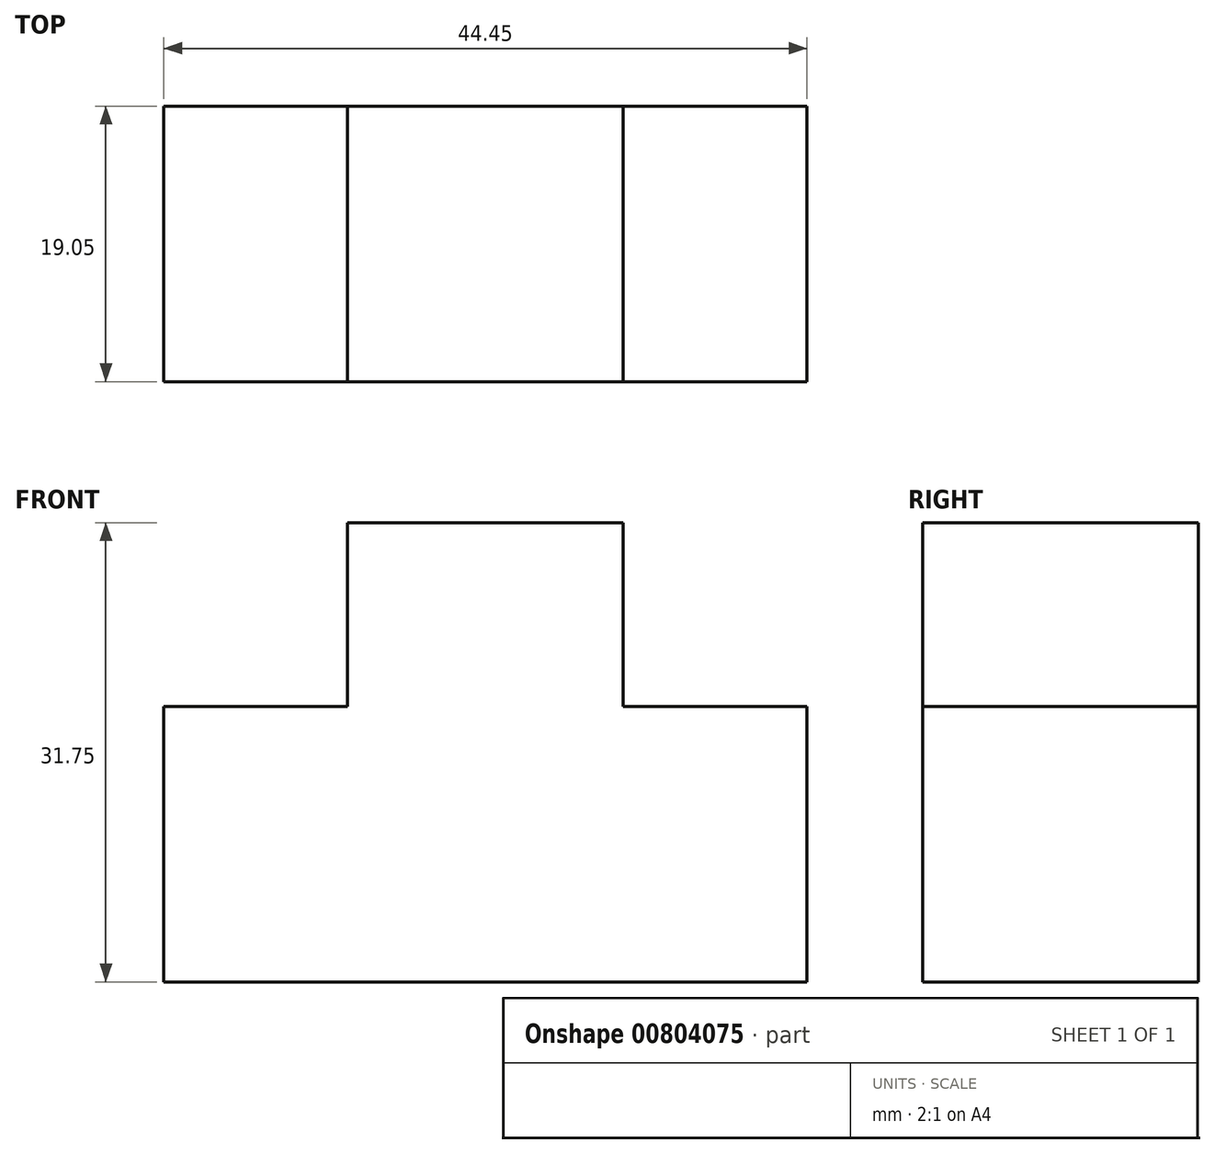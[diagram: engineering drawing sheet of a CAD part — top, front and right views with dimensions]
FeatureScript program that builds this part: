
annotation { "Feature Type Name" : "Feature", "Feature Type Description" : "" }
export const myFeature = defineFeature(function(context is Context, id is Id, definition is map)
    precondition{}
    {
        {
            var Q0;
            Q0=qCreatedBy(makeId("Front.planeOp"),FACE);
            var sketch = newSketch(context, id + "F0", { "sketchPlane" : qUnion([Q0])});
            skLineSegment(sketch, "E0", {"start": v(0, 0) * mm, "end": v(44.45, 0) * mm});
            skLineSegment(sketch, "E1", {"start": v(44.45, 0) * mm, "end": v(44.45, 19.05) * mm});
            skLineSegment(sketch, "E2", {"start": v(44.45, 19.05) * mm, "end": v(31.75, 19.05) * mm});
            skLineSegment(sketch, "E3", {"start": v(31.75, 19.05) * mm, "end": v(31.75, 31.75) * mm});
            skLineSegment(sketch, "E4", {"start": v(31.75, 31.75) * mm, "end": v(12.7, 31.75) * mm});
            skLineSegment(sketch, "E5", {"start": v(12.7, 31.75) * mm, "end": v(12.7, 19.05) * mm});
            skLineSegment(sketch, "E6", {"start": v(12.7, 19.05) * mm, "end": v(0, 19.05) * mm});
            skLineSegment(sketch, "E7", {"start": v(0, 19.05) * mm, "end": v(0, 0) * mm});
            skSolve(sketch);
        }
        {
            var Q0;
            Q0=makeQuery(id+"F0.imprint","IMPRINT",FACE,{"disambiguationData":[TD([[makeQuery(id+"F0.imprint","IMPRINT",EDGE,{"derivedFrom":sQuery(id+"F0.wireOp",EDGE,"E0")}),1.0]])]});
            extrude(context, id + "F1", {"entities" : qUnion([Q0]), "depth" : 19.05 * mm, "offsetDistance" : 25.4 * mm});
        }
    });
